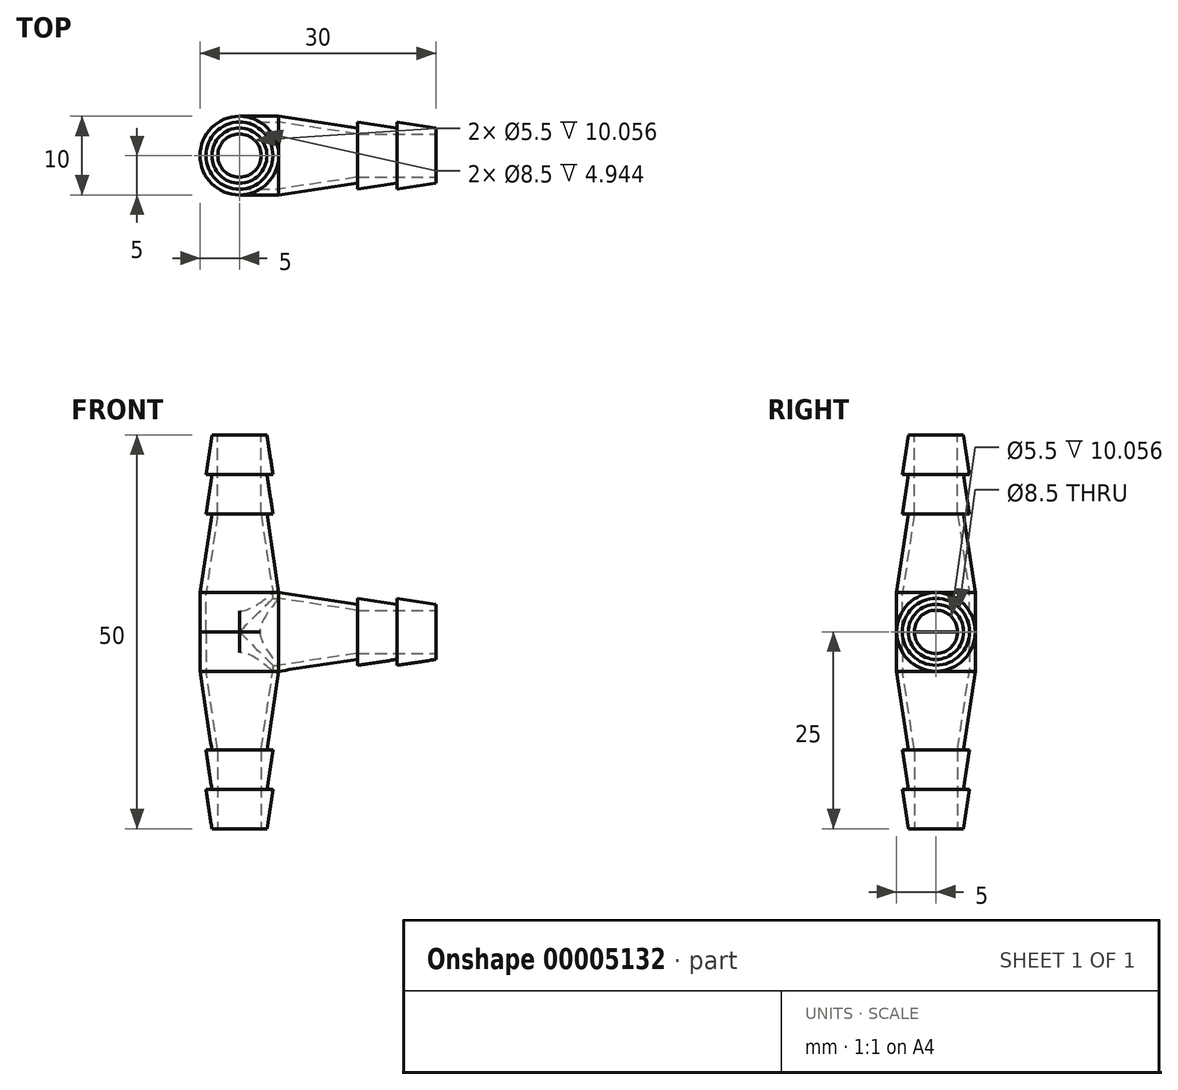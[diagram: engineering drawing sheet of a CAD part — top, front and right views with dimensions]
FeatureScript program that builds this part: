
annotation { "Feature Type Name" : "Feature", "Feature Type Description" : "" }
export const myFeature = defineFeature(function(context is Context, id is Id, definition is map)
    precondition{}
    {
        {
            var Q0;
            Q0=qCreatedBy(makeId("Front.planeOp"),FACE);
            var sketch = newSketch(context, id + "F0", { "sketchPlane" : qUnion([Q0])});
            skLineSegment(sketch, "E0", {"start": v(0, 0) * mm, "end": v(0, -25) * mm, "construction": true});
            skLineSegment(sketch, "E1", {"start": v(2.75, 0) * mm, "end": v(3.5, 0) * mm});
            skLineSegment(sketch, "E2", {"start": v(3.5, 0) * mm, "end": v(4.25, -5) * mm});
            skLineSegment(sketch, "E3", {"start": v(3.5, 0) * mm, "end": v(3.5, -5) * mm, "construction": true});
            skLineSegment(sketch, "E4", {"start": v(3.5, -5) * mm, "end": v(3.5, -10) * mm, "construction": true});
            skLineSegment(sketch, "E5", {"start": v(4.25, -5) * mm, "end": v(3.5, -5) * mm});
            skLineSegment(sketch, "E6", {"start": v(3.5, -5) * mm, "end": v(4.25, -10) * mm});
            skLineSegment(sketch, "E7", {"start": v(4.25, -10) * mm, "end": v(3.5, -10) * mm});
            skLineSegment(sketch, "E8", {"start": v(2.75, 0) * mm, "end": v(2.75, -10.06) * mm});
            skLineSegment(sketch, "E9", {"start": v(3.5, -10) * mm, "end": v(5, -20) * mm});
            skLineSegment(sketch, "E10", {"start": v(2.75, -10.06) * mm, "end": v(4.25, -20.06) * mm});
            skLineSegment(sketch, "E11", {"start": v(3.5, -15.06) * mm, "end": v(4.24, -14.94) * mm});
            skLineSegment(sketch, "E12", {"start": v(5, -20) * mm, "end": v(5, -25) * mm});
            skLineSegment(sketch, "E13", {"start": v(5, -25) * mm, "end": v(4.25, -25) * mm});
            skLineSegment(sketch, "E14", {"start": v(4.25, -25) * mm, "end": v(4.25, -20.06) * mm});
            skSolve(sketch);
        }
        {
            var Q0;
            Q0=makeQuery(id+"F0.imprint","IMPRINT",FACE,{"disambiguationData":[TD([[makeQuery(id+"F0.imprint","IMPRINT",EDGE,{"derivedFrom":sQuery(id+"F0.wireOp",EDGE,"E1")}),-1.0]])]});
            var Q1;
            {var subQ2=sQuery(id+"F0.wireOp",EDGE,"E11");Q1=makeQuery(id+"F0.imprint","IMPRINT",FACE,{"disambiguationData":[TD([[makeQuery(id+"F0.imprint","IMPRINT",EDGE,{"derivedFrom":subQ2}),-1.0]])]});}
            var Q2;
            Q2=sQuery(id+"F0.wireOp",EDGE,"E0");
            revolve(context, id + "F1", {"entities" : qUnion([Q0, Q1]), "axis" : qUnion([Q2]), "revolveType" : RevolveType.FULL});
        }
        {
            var Q0;
            Q0=makeQuery(id+"F1.opRevolve","SWEPT_FACE",FACE,{"disambiguationData":[OSD([sQuery(id+"F0.wireOp",EDGE,"E13")])]});
            cPlane(context, id + "F2", {"entities" : qUnion([Q0]), "cplaneType" : CPlaneType.OFFSET, "offset" : 0 * mm, "width" : 150 * mm, "height" : 150 * mm});
        }
        {
            var Q0;
            Q0=qCreatedBy(id+"F2.planeOp",FACE);
            var sketch = newSketch(context, id + "F3", { "sketchPlane" : qUnion([Q0])});
            skLineSegment(sketch, "E15", {"start": v(0, 5) * mm, "end": v(0, -5) * mm, "construction": true});
            skSolve(sketch);
        }
        {
            var Q0;
            Q0=makeQuery(id+"F1.opRevolve","SWEPT_BODY",BODY,{"disambiguationData":[OSD([sQuery(id+"F0.wireOp",EDGE,"E1"),sQuery(id+"F0.wireOp",EDGE,"E2"),sQuery(id+"F0.wireOp",EDGE,"E5"),sQuery(id+"F0.wireOp",EDGE,"E6"),sQuery(id+"F0.wireOp",EDGE,"E7"),sQuery(id+"F0.wireOp",EDGE,"E8"),sQuery(id+"F0.wireOp",EDGE,"E9"),sQuery(id+"F0.wireOp",EDGE,"E10"),sQuery(id+"F0.wireOp",EDGE,"E12"),sQuery(id+"F0.wireOp",EDGE,"E13"),sQuery(id+"F0.wireOp",EDGE,"E14")])]});
            var Q1;
            Q1=sQuery(id+"F3.wireOp",EDGE,"E15");
            circularPattern(context, id + "F4", {"entities" : qUnion([Q0]), "axis" : qUnion([Q1]), "angle" : 90 * degree, "instanceCount" : 3});
        }
        {
            var Q0;
            Q0=qCreatedBy(makeId("Top.planeOp"),FACE);
            cPlane(context, id + "F5", {"entities" : qUnion([Q0]), "cplaneType" : CPlaneType.OFFSET, "offset" : 20 * mm, "oppositeDirection" : true, "width" : 150 * mm, "height" : 150 * mm});
        }
        {
            var Q0;
            Q0=qCreatedBy(id+"F5.planeOp",FACE);
            var sketch = newSketch(context, id + "F6", { "sketchPlane" : qUnion([Q0])});
            skCircle(sketch, "E16", {"center": v(0, 0) * mm, "radius": 4.25 * mm});
            skSolve(sketch);
        }
        {
            var Q0;
            Q0 = qSketchRegion(id + "F6", true);
            extrude(context, id + "F7", {"entities" : qUnion([Q0]), "operationType" : NewBodyOperationType.REMOVE, "oppositeDirection" : true, "depth" : 10 * mm});
        }
        {
            var Q0;
            Q0=makeQuery(id+"F4.opPattern","COPY",FACE,{"derivedFrom":makeQuery(id+"F1.opRevolve","SWEPT_FACE",FACE,{"disambiguationData":[OSD([sQuery(id+"F0.wireOp",EDGE,"E1")])]}),"instanceName":"1"});
            cPlane(context, id + "F8", {"entities" : qUnion([Q0]), "cplaneType" : CPlaneType.OFFSET, "offset" : 20 * mm, "oppositeDirection" : true, "width" : 150 * mm, "height" : 150 * mm});
        }
        {
            var Q0;
            Q0=qCreatedBy(id+"F8.planeOp",FACE);
            var sketch = newSketch(context, id + "F9", { "sketchPlane" : qUnion([Q0])});
            skCircle(sketch, "E17", {"center": v(0, -25) * mm, "radius": 4.25 * mm});
            skSolve(sketch);
        }
        {
            var Q0;
            Q0 = qSketchRegion(id + "F9", true);
            extrude(context, id + "F10", {"entities" : qUnion([Q0]), "operationType" : NewBodyOperationType.REMOVE, "oppositeDirection" : true, "depth" : 5 * mm});
        }
    });
